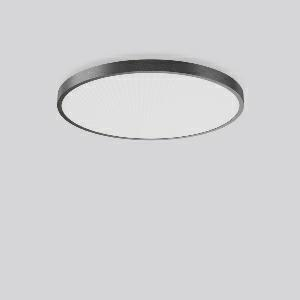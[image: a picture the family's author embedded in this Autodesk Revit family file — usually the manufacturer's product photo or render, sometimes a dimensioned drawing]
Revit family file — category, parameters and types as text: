
# Revit family: triona_round_a_312299_0031_2_730_79fa
name_source: partatom
category: Lighting Fixtures
units: mm (PartAtom-declared; Revit-internal decimal feet)

## family parameters
Cut with Voids When Loaded = No
Host = Face
Light Source = No
Part Type = Normal
Room Calculation Point = No
Round Connector Dimension = Use Diameter
Shared = No

## types (1)
- TuneableWhite 846 (1 x LED Modul 846, 5050 lm, 4600)
    Apparent Load = 49 VA
    CIE Flux Codes = 58 86 97 100 100
    Color Rendering = 80
    Color Temperature = 4600
    Default Elevation = 1800 mm
    Description = Series: TRIONA round
Decorative round LED surface-mounted luminaire. Flat, seamless frame: aluminium extrusion profile, powder coated. Cover made of sheet steel, powder-coated. Light emission through a diffuser in plastic, opal/prismatic. Lightguide and diffuser made of non-yellowing plastic (PMMA). Lateral light emission (RZB SIDELITE technology) for above-average homogeneous light distribution. Tunable white versions, dynamically adjustable from 2700 K to 6500 K. Suitable for Ceiling mounting, Wall (surface). Tool-free mounting via bayonet connection. Electronic ballast included. Very easy installation thanks to Plug+Play connection. With Casambi smart+free Bluetooth control for wireless network and operation using Android / iOS devices, free app available for download. Perfect for office areas (RUG < 19) and environments with computer screens in accordance with EN 12464-1. Ideal for use as part of the Human Centric Lighting concept in connection with RZB light management systems. 
Colour: anthracite metallic (DB703)
Diameter: 845 mm
Height: 88 mm
Lamp: LED
Socket: without socket
Colour temperature: 2700K - 6500K
Colour rendering index (CRI): 80
System power: 49 W
Rated luminous flux: 5050 lm
Luminous efficiency: 103 lm/W
System power 2: 51 W
Rated luminous flux 2: 4800 lm
Luminous efficiency 2: 94 lm/W
System power 3: 51 W
Rated luminous flux 3: 4900 lm
Luminous efficiency 3: 96 lm/W
Control gear: Dimmable Bluetooth converter
Protection class: I
Type of protection: IP 20
    Height = 88 mm
    Lamp = 1 x LED Modul 846
    Lamp Light Flux = 5050 lm
    Lamp count = 1
    Length = 845 mm
    Lifetime = 50000 h
    Luminous efficacy = 103 lm/W
    Manufacturer = RZB
    ModVariant = No
    Model = 312299.0031.2.730
    Mounting Place = Ceiling
    Mounting Type = Surface mounted
    Number of Poles = 1
    OnlyDefault = Yes
    Power Factor = 1
    Product Name = TRIONA round A
    Product group = Surface mounted modular luminaires
    ProductGroupID = 306
    Protection Class = Protection class I
    Protection Degree = IP 20
    RLX_Detail_Level = 1
    RLX_Emergency_Light_Flux = 0 lm
    RLX_Emergency_Type = 0
    RLX_Emergency_Type_DB = No
    RlxData = <blob elided: 39117 chars, md5=b3677272>
    Socket = socket
    Standby Power = 0 W
    System Light Flux = 5050 lm
    System Power = 49 W
    Type Comments = TuneableWhite 846
    Type Image = 312300.0031.jpg
    URL = http://relux.com
    VarID = tuneablewhite_846
    Voltage = 230 V
    Voltage Range = 220-240 V
    Weight = 0.00 kg
    Width = 0 mm  [stored 0 ft]

note: [stored X ft] marks values corroborated as IEEE doubles in the binary element streams (Revit-internal decimal feet)

## geometry (parser evidence)
native form markers: Blend x4, Sweep x12
no freeform markers — native parametric forms only
